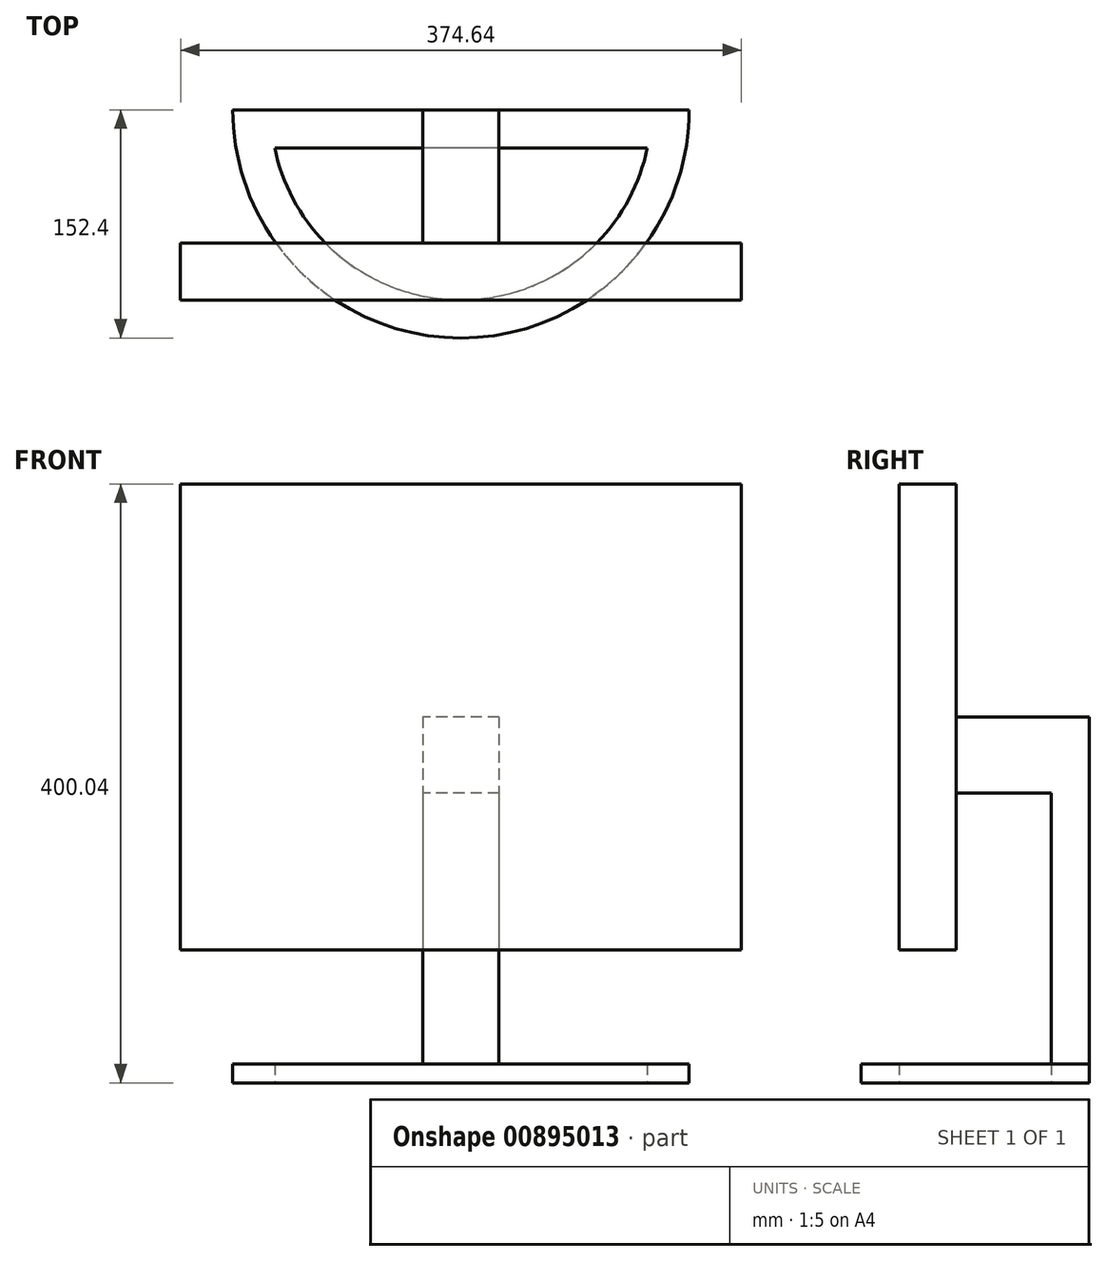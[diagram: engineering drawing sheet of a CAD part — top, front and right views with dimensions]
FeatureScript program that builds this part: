
annotation { "Feature Type Name" : "Feature", "Feature Type Description" : "" }
export const myFeature = defineFeature(function(context is Context, id is Id, definition is map)
    precondition{}
    {
        {
            var Q0;
            Q0=qCreatedBy(makeId("Front.planeOp"),FACE);
            var sketch = newSketch(context, id + "F0", { "sketchPlane" : qUnion([Q0])});
            skLineSegment(sketch, "E0.bottom", {"start": v(187.33, 155.58) * mm, "end": v(-187.33, 155.58) * mm});
            skLineSegment(sketch, "E0.top", {"start": v(187.33, -155.58) * mm, "end": v(-187.33, -155.58) * mm});
            skLineSegment(sketch, "E0.left", {"start": v(187.33, 155.58) * mm, "end": v(187.33, -155.58) * mm});
            skLineSegment(sketch, "E0.right", {"start": v(-187.33, 155.58) * mm, "end": v(-187.33, -155.58) * mm});
            skPoint(sketch, "E0.middle", {"position": v(0, 0) * mm});
            skSolve(sketch);
        }
        {
            var Q0;
            Q0=makeQuery(id+"F0.imprint","IMPRINT",FACE,{"disambiguationData":[TD([[makeQuery(id+"F0.imprint","IMPRINT",EDGE,{"derivedFrom":sQuery(id+"F0.wireOp",EDGE,"E0.bottom")}),1.0]])]});
            extrude(context, id + "F1", {"entities" : qUnion([Q0]), "depth" : 38.1 * mm, "offsetDistance" : 25.4 * mm});
        }
        {
            var Q0;
            Q0=makeQuery(id+"F1.opExtrude","CAP_FACE",FACE,{"disambiguationData":[OSD([sQuery(id+"F0.wireOp",EDGE,"E0.bottom"),sQuery(id+"F0.wireOp",EDGE,"E0.top"),sQuery(id+"F0.wireOp",EDGE,"E0.left"),sQuery(id+"F0.wireOp",EDGE,"E0.right")])],"isStart":true});
            var sketch = newSketch(context, id + "F2", { "sketchPlane" : qUnion([Q0])});
            skPoint(sketch, "E1.firstSnap0", {"position": v(187.33, 0) * mm});
            skLineSegment(sketch, "E1.bottom", {"start": v(-25.4, 0) * mm, "end": v(25.4, 0) * mm});
            skLineSegment(sketch, "E1.top", {"start": v(-25.4, -244.48) * mm, "end": v(25.4, -244.48) * mm});
            skLineSegment(sketch, "E1.left", {"start": v(-25.4, 0) * mm, "end": v(-25.4, -244.48) * mm});
            skLineSegment(sketch, "E1.right", {"start": v(25.4, 0) * mm, "end": v(25.4, -244.48) * mm});
            skSolve(sketch);
        }
        {
            var Q0;
            {var subQ0=sQuery(id+"F2.wireOp",EDGE,"E1.top");Q0=makeQuery(id+"F2.imprint","IMPRINT",FACE,{"disambiguationData":[TD([[makeQuery(id+"F2.imprint","IMPRINT",EDGE,{"derivedFrom":subQ0}),1.0]])]});}
            var Q1;
            {var subQ0=sQuery(id+"F2.wireOp",EDGE,"E1.bottom");Q1=makeQuery(id+"F2.imprint","IMPRINT",FACE,{"disambiguationData":[TD([[makeQuery(id+"F2.imprint","IMPRINT",EDGE,{"derivedFrom":subQ0}),-1.0]])]});}
            extrude(context, id + "F3", {"entities" : qUnion([Q0, Q1]), "operationType" : NewBodyOperationType.ADD, "depth" : 88.9 * mm, "offsetDistance" : 25.4 * mm});
        }
        {
            var Q0;
            Q0=makeQuery(id+"F3.opExtrude","SWEPT_FACE",FACE,{"disambiguationData":[OSD([sQuery(id+"F2.wireOp",EDGE,"E1.right")])]});
            var sketch = newSketch(context, id + "F4", { "sketchPlane" : qUnion([Q0])});
            skLineSegment(sketch, "E2.bottom", {"start": v(-63.5, -50.8) * mm, "end": v(0, -50.8) * mm});
            skLineSegment(sketch, "E2.top", {"start": v(-63.5, -244.48) * mm, "end": v(0, -244.48) * mm});
            skLineSegment(sketch, "E2.left", {"start": v(-63.5, -50.8) * mm, "end": v(-63.5, -244.48) * mm});
            skLineSegment(sketch, "E2.right", {"start": v(0, -50.8) * mm, "end": v(0, -244.48) * mm});
            skSolve(sketch);
        }
        {
            var Q0;
            Q0 = qSketchRegion(id + "F4", true);
            extrude(context, id + "F5", {"entities" : qUnion([Q0]), "operationType" : NewBodyOperationType.REMOVE, "endBound" : BoundingType.THROUGH_ALL, "oppositeDirection" : true, "depth" : 25.4 * mm, "offsetDistance" : 25.4 * mm});
        }
        {
            var Q0;
            Q0=makeQuery(id+"F3.opExtrude","SWEPT_FACE",FACE,{"disambiguationData":[OSD([sQuery(id+"F2.wireOp",EDGE,"E1.top")])]});
            var sketch = newSketch(context, id + "F6", { "sketchPlane" : qUnion([Q0])});
            skArc(sketch, "E3", {"start": v(152.4, -88.9) * mm, "mid": v(0, 63.5) * mm, "end": v(-152.4, -88.9) * mm});
            skLineSegment(sketch, "E4", {"start": v(-152.4, -88.9) * mm, "end": v(152.4, -88.9) * mm});
            skArc(sketch, "E5", {"start": v(124.43, -63.5) * mm, "mid": v(0, 38.1) * mm, "end": v(-124.43, -63.5) * mm});
            skLineSegment(sketch, "E6", {"start": v(-124.43, -63.5) * mm, "end": v(124.43, -63.5) * mm});
            skSolve(sketch);
        }
        {
            var Q0;
            {var subQ4=sQuery(id+"F6.wireOp",EDGE,"E3");Q0=makeQuery(id+"F6.imprint","IMPRINT",FACE,{"disambiguationData":[TD([[makeQuery(id+"F6.imprint","IMPRINT",EDGE,{"derivedFrom":subQ4}),1.0]])]});}
            extrude(context, id + "F7", {"entities" : qUnion([Q0]), "operationType" : NewBodyOperationType.ADD, "oppositeDirection" : true, "depth" : 12.7 * mm, "offsetDistance" : 25.4 * mm});
        }
    });
